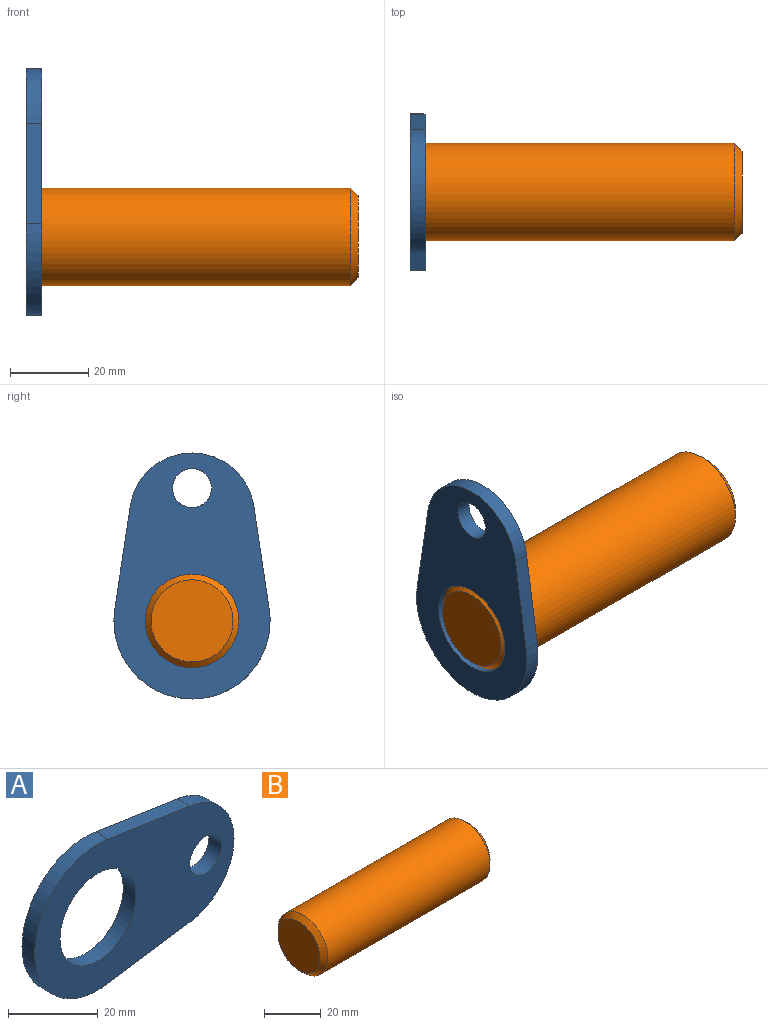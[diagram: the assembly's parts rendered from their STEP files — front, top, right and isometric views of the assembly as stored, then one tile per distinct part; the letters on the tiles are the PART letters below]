
ASSEMBLY  parts=2 mates=1
PART A: 8 faces, bbox 63x4x40 mm
  f0: plane 25.61x4mm, normal (0.15,0,-0.99), area 103.6mm2, adj f1,f5,f6,f7
  f1: cylinder r=16mm len=31.73mm, axis (0,-1,0), area 184.5mm2, adj f0,f2,f6,f7
  f2: plane 26.11x4.01mm, normal (0.15,0,0.99), area 104.6mm2, adj f1,f5,f6,f7
  f3: cylinder r=5mm len=10mm, axis (0,-1,0), area 125.7mm2, adj f6,f7
  f4: cylinder r=12mm len=24mm, axis (0,-1,0), area 301.6mm2, adj f6,f7
  f5: cylinder r=20mm len=40mm, axis (0,-1,0), area 278.1mm2, adj f0,f2,f6,f7
  f6: plane 63x40mm, normal (0,-1,0), area 1482mm2, adj f0,f1,f2,f3,f4,f5
  f7: plane 63x40mm, normal (0,1,0), area 1482mm2, adj f0,f1,f2,f3,f4,f5
PART B: 5 faces, bbox 85x25x25 mm
  f0: cylinder r=12.5mm len=81mm, axis (-1,0,0), area 6361.7mm2, adj f3,f4
  f1: plane 21x21mm, normal (1,0,0), area 346.4mm2, adj f4
  f2: plane 21x21mm, normal (-1,0,0), area 346.4mm2, adj f3
  f3: cone r=12.5mm half-angle=45deg, axis (1,0,0), area 204.4mm2, adj f0,f2
  f4: cone r=10.5mm half-angle=45deg, axis (-1,0,0), area 204.4mm2, adj f0,f1
PLACE A rot(axis=(-0.58,-0.58,-0.58),120deg) t=(4,-29,-21)mm
PLACE B at identity
MATE fastened A.f4 <-> B.f0  axis (-1,0,0) through (0,0,0)mm
